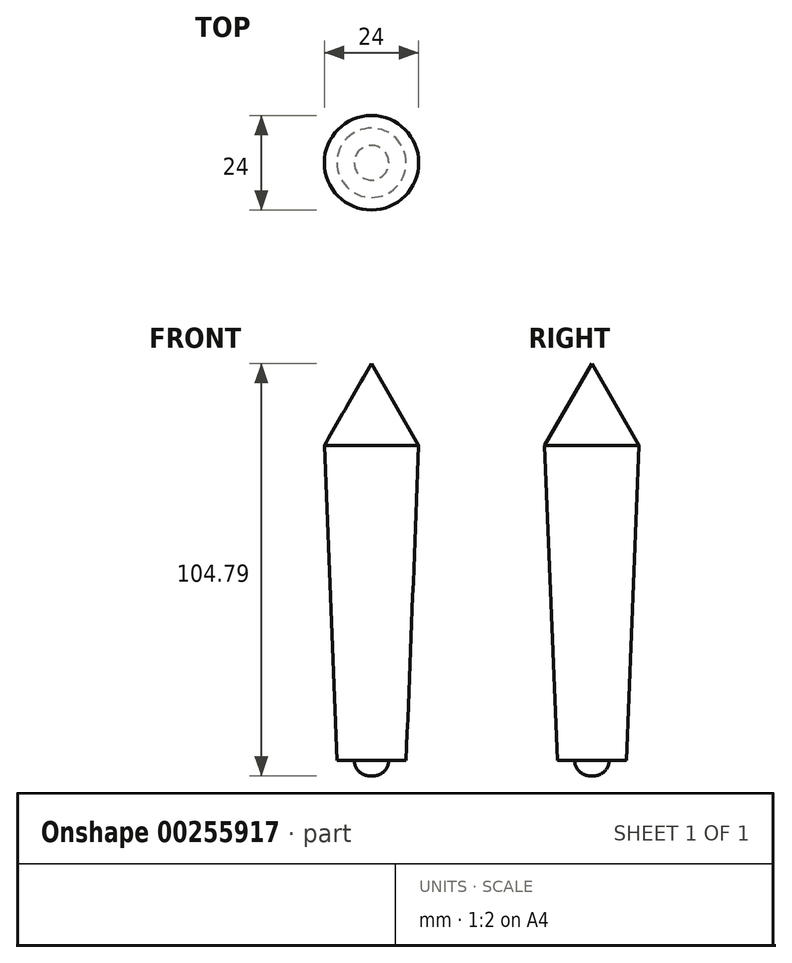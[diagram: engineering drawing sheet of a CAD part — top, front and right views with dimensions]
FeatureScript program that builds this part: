
annotation { "Feature Type Name" : "Feature", "Feature Type Description" : "" }
export const myFeature = defineFeature(function(context is Context, id is Id, definition is map)
    precondition{}
    {
        {
            var Q0;
            Q0=qCreatedBy(makeId("Front.planeOp"),FACE);
            var sketch = newSketch(context, id + "F0", { "sketchPlane" : qUnion([Q0])});
            skLineSegment(sketch, "E0", {"start": v(0, 50.4) * mm, "end": v(12, 29.62) * mm});
            skLineSegment(sketch, "E1", {"start": v(12, 29.62) * mm, "end": v(8.8, -50.38) * mm});
            skLineSegment(sketch, "E2", {"start": v(8.8, -50.38) * mm, "end": v(0, -50.38) * mm});
            skLineSegment(sketch, "E3", {"start": v(4.4, -50.38) * mm, "end": v(4.4, -54.38) * mm});
            skLineSegment(sketch, "E4", {"start": v(4.4, -54.38) * mm, "end": v(0, -54.38) * mm});
            skLineSegment(sketch, "E5", {"start": v(12, 29.62) * mm, "end": v(0, 29.62) * mm});
            skLineSegment(sketch, "E6", {"start": v(0, 50.4) * mm, "end": v(0, -54.38) * mm});
            skSolve(sketch);
        }
        {
            var Q0;
            {var subQ0=sQuery(id+"F0.wireOp",EDGE,"E0");Q0=makeQuery(id+"F0.imprint","IMPRINT",FACE,{"disambiguationData":[TD([[makeQuery(id+"F0.imprint","IMPRINT",EDGE,{"derivedFrom":subQ0}),-1.0]])]});}
            var Q1;
            {var subQ5=sQuery(id+"F0.wireOp",EDGE,"E1");Q1=makeQuery(id+"F0.imprint","IMPRINT",FACE,{"disambiguationData":[TD([[makeQuery(id+"F0.imprint","IMPRINT",EDGE,{"derivedFrom":subQ5}),-1.0]])]});}
            var Q2;
            {var subQ3=sQuery(id+"F0.wireOp",EDGE,"E3");Q2=makeQuery(id+"F0.imprint","IMPRINT",FACE,{"disambiguationData":[TD([[makeQuery(id+"F0.imprint","IMPRINT",EDGE,{"derivedFrom":subQ3}),-1.0]])]});}
            var Q3;
            Q3=sQuery(id+"F0.wireOp",EDGE,"E6");
            revolve(context, id + "F1", {"entities" : qUnion([Q0, Q1, Q2]), "axis" : qUnion([Q3]), "revolveType" : RevolveType.FULL});
        }
        {
            var Q0;
            Q0=makeQuery(id+"F1.opRevolve","SWEPT_EDGE",EDGE,{"disambiguationData":[OSD([sQuery(id+"F0.wireOp",EDGE,"E3"),sQuery(id+"F0.wireOp",EDGE,"E4")])]});
            fillet(context, id + "F2", {"entities" : qUnion([Q0]), "radius" : 4 * mm, "tangentPropagation" : true, "allowEdgeOverflow" : false});
        }
    });
